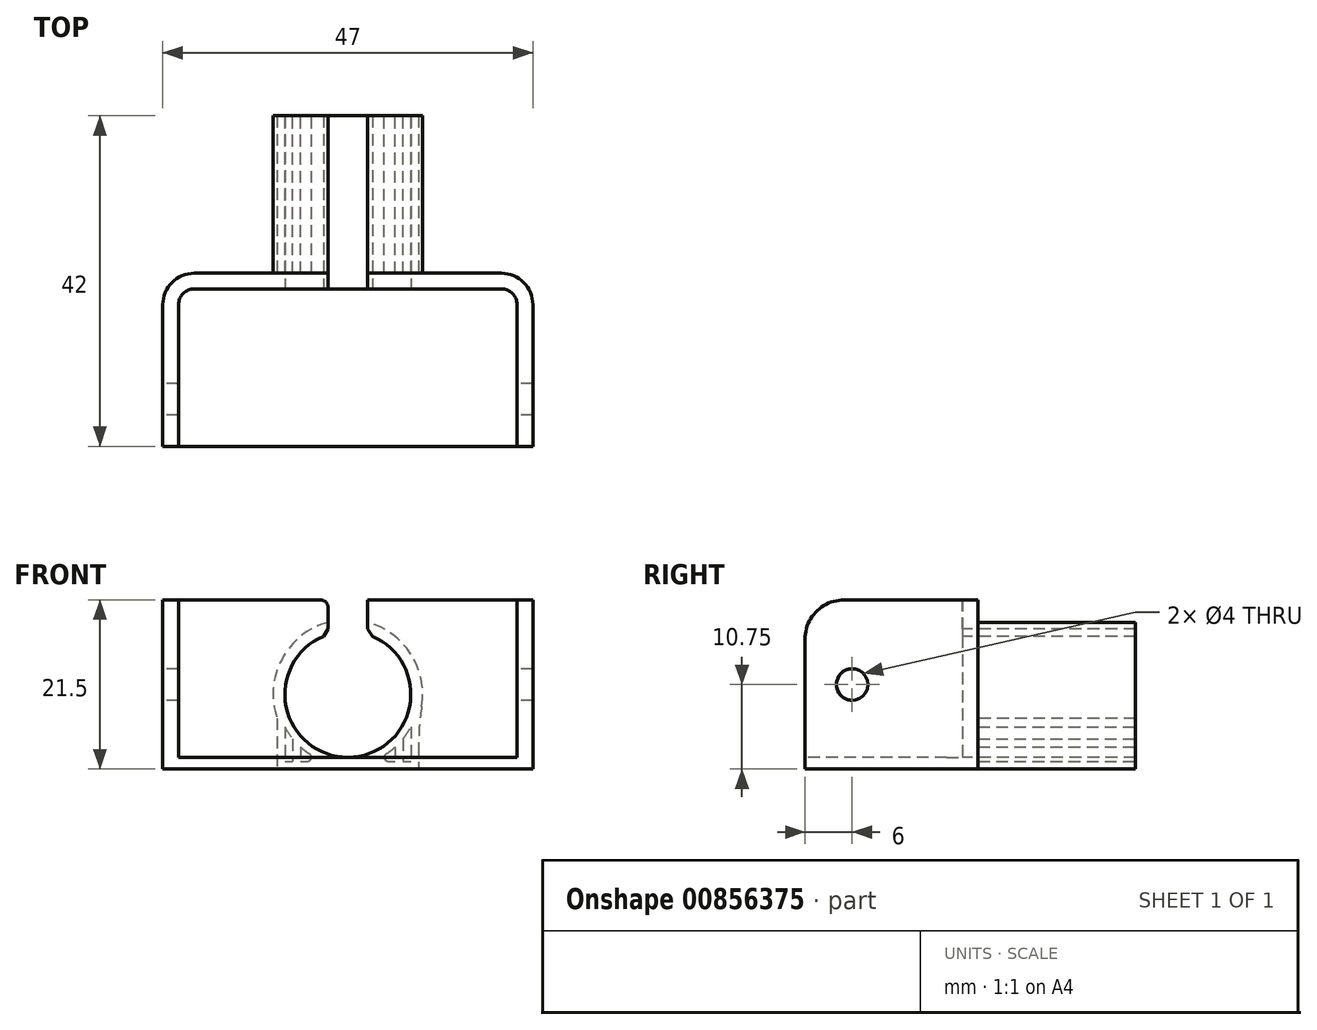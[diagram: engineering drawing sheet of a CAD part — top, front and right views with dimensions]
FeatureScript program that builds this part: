
annotation { "Feature Type Name" : "Feature", "Feature Type Description" : "" }
export const myFeature = defineFeature(function(context is Context, id is Id, definition is map)
    precondition{}
    {
        {
            var Q0;
            Q0=qCreatedBy(makeId("Top.planeOp"),FACE);
            var sketch = newSketch(context, id + "F0", { "sketchPlane" : qUnion([Q0])});
            skLineSegment(sketch, "E0.bottom", {"start": v(21.5, 20) * mm, "end": v(-21.5, 20) * mm});
            skLineSegment(sketch, "E0.left", {"start": v(21.5, 20) * mm, "end": v(21.5, 0) * mm});
            skLineSegment(sketch, "E0.right", {"start": v(-21.5, 20) * mm, "end": v(-21.5, 0) * mm});
            skPoint(sketch, "E0.middle", {"position": v(0, 0) * mm});
            skLineSegment(sketch, "E1.bottom", {"start": v(23.5, 22) * mm, "end": v(-23.5, 22) * mm});
            skLineSegment(sketch, "E1.left", {"start": v(23.5, 22) * mm, "end": v(23.5, 0) * mm});
            skLineSegment(sketch, "E1.right", {"start": v(-23.5, 22) * mm, "end": v(-23.5, 0) * mm});
            skLineSegment(sketch, "E2", {"start": v(-23.5, 0) * mm, "end": v(-21.5, 0) * mm});
            skPoint(sketch, "E0.top.end.orphan", {"position": v(-21.5, -20) * mm});
            skPoint(sketch, "E1.top.end.orphan", {"position": v(-23.5, -22) * mm});
            skPoint(sketch, "E3.orphan", {"position": v(21.5, -20) * mm});
            skPoint(sketch, "E4.orphan", {"position": v(23.5, -22) * mm});
            skLineSegment(sketch, "E5.trimOffspring", {"start": v(21.5, 0) * mm, "end": v(23.5, 0) * mm});
            skSolve(sketch);
        }
        {
            var Q0;
            Q0=makeQuery(id+"F0.imprint","IMPRINT",FACE,{"disambiguationData":[TD([[makeQuery(id+"F0.imprint","IMPRINT",EDGE,{"derivedFrom":sQuery(id+"F0.wireOp",EDGE,"E0.bottom")}),-1.0]])]});
            extrude(context, id + "F1", {"entities" : qUnion([Q0]), "depth" : 20 * mm, "offsetDistance" : 25 * mm});
        }
        {
            var Q0;
            Q0=makeQuery(id+"F1.opExtrude","SWEPT_EDGE",EDGE,{"disambiguationData":[OSD([sQuery(id+"F0.wireOp",EDGE,"E0.bottom"),sQuery(id+"F0.wireOp",EDGE,"E0.right")])]});
            var Q1;
            Q1=makeQuery(id+"F1.opExtrude","SWEPT_EDGE",EDGE,{"disambiguationData":[OSD([sQuery(id+"F0.wireOp",EDGE,"E0.bottom"),sQuery(id+"F0.wireOp",EDGE,"E0.left")])]});
            fillet(context, id + "F2", {"entities" : qUnion([Q0, Q1]), "radius" : 2 * mm, "tangentPropagation" : true, "allowEdgeOverflow" : false});
        }
        {
            var Q0;
            Q0=makeQuery(id+"F1.opExtrude","SWEPT_EDGE",EDGE,{"disambiguationData":[OSD([sQuery(id+"F0.wireOp",EDGE,"E1.bottom"),sQuery(id+"F0.wireOp",EDGE,"E1.right")])]});
            var Q1;
            Q1=makeQuery(id+"F1.opExtrude","SWEPT_EDGE",EDGE,{"disambiguationData":[OSD([sQuery(id+"F0.wireOp",EDGE,"E1.bottom"),sQuery(id+"F0.wireOp",EDGE,"E1.left")])]});
            fillet(context, id + "F3", {"entities" : qUnion([Q0, Q1]), "radius" : 4 * mm, "tangentPropagation" : true, "allowEdgeOverflow" : false});
        }
        {
            var Q0;
            Q0=makeQuery(id+"F1.opExtrude","CAP_FACE",FACE,{"disambiguationData":[OSD([sQuery(id+"F0.wireOp",EDGE,"E0.bottom"),sQuery(id+"F0.wireOp",EDGE,"E0.left"),sQuery(id+"F0.wireOp",EDGE,"E0.right"),sQuery(id+"F0.wireOp",EDGE,"E1.bottom"),sQuery(id+"F0.wireOp",EDGE,"E1.left"),sQuery(id+"F0.wireOp",EDGE,"E1.right"),sQuery(id+"F0.wireOp",EDGE,"E2"),sQuery(id+"F0.wireOp",EDGE,"E5.trimOffspring")])],"isStart":true});
            var sketch = newSketch(context, id + "F4", { "sketchPlane" : qUnion([Q0])});
            skLineSegment(sketch, "E6.0", {"start": v(23.5, -18) * mm, "end": v(23.5, 0) * mm});
            skArc(sketch, "E6.1", {"start": v(19.5, -22) * mm, "mid": v(22.33, -20.83) * mm, "end": v(23.5, -18) * mm});
            skLineSegment(sketch, "E6.2", {"start": v(19.5, -22) * mm, "end": v(-19.5, -22) * mm});
            skArc(sketch, "E6.3", {"start": v(-23.5, -18) * mm, "mid": v(-22.33, -20.83) * mm, "end": v(-19.5, -22) * mm});
            skLineSegment(sketch, "E6.4", {"start": v(-23.5, -18) * mm, "end": v(-23.5, 0) * mm});
            skLineSegment(sketch, "E7", {"start": v(23.5, 0) * mm, "end": v(-23.5, 0) * mm});
            skPoint(sketch, "E8.orphan", {"position": v(23.5, 0) * mm});
            skPoint(sketch, "E9.orphan", {"position": v(-23.5, 0) * mm});
            skSolve(sketch);
        }
        {
            var Q0;
            {var subQ0=sQuery(id+"F0.wireOp",EDGE,"E0.bottom");Q0=makeQuery(id+"F4.imprint","IMPRINT",FACE,{"disambiguationData":[TD([[makeQuery(id+"F4.imprint","IMPRINT",EDGE,{"derivedFrom":makeQuery(id+"F1.opExtrude","CAP_EDGE",EDGE,{"disambiguationData":[OSD([subQ0])],"isStart":true})}),-1.0]])]});}
            var Q1;
            {var subQ11=sQuery(id+"F4.wireOp",EDGE,"E6.0");Q1=makeQuery(id+"F4.imprint","IMPRINT",FACE,{"disambiguationData":[TD([[makeQuery(id+"F4.imprint","IMPRINT",EDGE,{"derivedFrom":subQ11}),1.0]])]});}
            extrude(context, id + "F5", {"entities" : qUnion([Q0, Q1]), "operationType" : NewBodyOperationType.ADD, "depth" : 1.5 * mm, "offsetDistance" : 25 * mm});
        }
        {
            var Q0;
            Q0=makeQuery(id+"F5.boolean.opBoolean","MERGE",FACE,{"derivedFrom":[makeQuery(id+"F1.opExtrude","SWEPT_FACE",FACE,{"disambiguationData":[OSD([sQuery(id+"F0.wireOp",EDGE,"E1.bottom")])]}),makeQuery(id+"F5.opExtrude","SWEPT_FACE",FACE,{"disambiguationData":[OSD([sQuery(id+"F4.wireOp",EDGE,"E6.2")])]})]});
            var sketch = newSketch(context, id + "F6", { "sketchPlane" : qUnion([Q0])});
            skCircle(sketch, "E10", {"center": v(0, 8) * mm, "radius": 8 * mm});
            skCircle(sketch, "E11", {"center": v(0, 8) * mm, "radius": 9.5 * mm});
            skSolve(sketch);
        }
        {
            var Q0;
            Q0=makeQuery(id+"F6.imprint","IMPRINT",FACE,{"disambiguationData":[TD([[makeQuery(id+"F6.imprint","IMPRINT",EDGE,{"derivedFrom":sQuery(id+"F6.wireOp",EDGE,"E10")}),-1.0]])]});
            extrude(context, id + "F7", {"entities" : qUnion([Q0]), "operationType" : NewBodyOperationType.ADD, "depth" : 20 * mm, "offsetDistance" : 25 * mm});
        }
        {
            var Q0;
            Q0=makeQuery(id+"F7.boolean.opBoolean","SPLIT",FACE,{"disambiguationData":[TD([makeQuery(id+"F7.opExtrude","SWEPT_FACE",FACE,{"disambiguationData":[OSD([sQuery(id+"F6.wireOp",EDGE,"E10")])]})])],"derivedFrom":makeQuery(id+"F5.boolean.opBoolean","MERGE",FACE,{"derivedFrom":[makeQuery(id+"F1.opExtrude","SWEPT_FACE",FACE,{"disambiguationData":[OSD([sQuery(id+"F0.wireOp",EDGE,"E1.bottom")])]}),makeQuery(id+"F5.opExtrude","SWEPT_FACE",FACE,{"disambiguationData":[OSD([sQuery(id+"F4.wireOp",EDGE,"E6.2")])]})]})});
            extrude(context, id + "F8", {"entities" : qUnion([Q0]), "operationType" : NewBodyOperationType.REMOVE, "oppositeDirection" : true, "depth" : 25 * mm, "offsetDistance" : 25 * mm});
        }
        {
            var Q0;
            Q0=makeQuery(id+"F1.opExtrude","CAP_FACE",FACE,{"disambiguationData":[OSD([sQuery(id+"F0.wireOp",EDGE,"E0.bottom"),sQuery(id+"F0.wireOp",EDGE,"E0.left"),sQuery(id+"F0.wireOp",EDGE,"E0.right"),sQuery(id+"F0.wireOp",EDGE,"E1.bottom"),sQuery(id+"F0.wireOp",EDGE,"E1.left"),sQuery(id+"F0.wireOp",EDGE,"E1.right"),sQuery(id+"F0.wireOp",EDGE,"E2"),sQuery(id+"F0.wireOp",EDGE,"E5.trimOffspring")])],"isStart":false});
            var sketch = newSketch(context, id + "F9", { "sketchPlane" : qUnion([Q0])});
            skLineSegment(sketch, "E12.bottom", {"start": v(-2.5, 16.96) * mm, "end": v(2.5, 16.96) * mm});
            skLineSegment(sketch, "E12.top", {"start": v(-2.5, 57.99) * mm, "end": v(2.5, 57.99) * mm});
            skLineSegment(sketch, "E12.left", {"start": v(-2.5, 16.96) * mm, "end": v(-2.5, 57.99) * mm});
            skLineSegment(sketch, "E12.right", {"start": v(2.5, 16.96) * mm, "end": v(2.5, 57.99) * mm});
            skPoint(sketch, "E12.middle", {"position": v(0, 37.47) * mm});
            skSolve(sketch);
        }
        {
            var Q0;
            {var subQ0=sQuery(id+"F9.wireOp",EDGE,"E12.top");Q0=makeQuery(id+"F9.imprint","IMPRINT",FACE,{"disambiguationData":[TD([[makeQuery(id+"F9.imprint","IMPRINT",EDGE,{"derivedFrom":subQ0}),-1.0]])]});}
            var Q1;
            {var subQ0=sQuery(id+"F9.wireOp",EDGE,"E12.bottom");Q1=makeQuery(id+"F9.imprint","IMPRINT",FACE,{"disambiguationData":[TD([[makeQuery(id+"F9.imprint","IMPRINT",EDGE,{"derivedFrom":subQ0}),1.0]])]});}
            var Q2;
            {var subQ0=sQuery(id+"F9.wireOp",EDGE,"E12.left");var subQ1=makeQuery(id+"F1.opExtrude","CAP_EDGE",EDGE,{"disambiguationData":[OSD([sQuery(id+"F0.wireOp",EDGE,"E0.bottom")])],"isStart":false});var subQ2=makeQuery(id+"F9.imprint","INTERSECT",VERTEX,{"derivedFrom":[subQ1,subQ0]});Q2=makeQuery(id+"F9.imprint","IMPRINT",FACE,{"disambiguationData":[TD([[makeQuery(id+"F9.imprint","IMPRINT",EDGE,{"disambiguationData":[TD([[subQ2,-1.0]])],"derivedFrom":subQ0}),-1.0]])]});}
            extrude(context, id + "F10", {"entities" : qUnion([Q0, Q1, Q2]), "operationType" : NewBodyOperationType.REMOVE, "oppositeDirection" : true, "depth" : 12.4 * mm, "offsetDistance" : 25 * mm});
        }
        {
            var Q0;
            {var subQ0=sQuery(id+"F6.wireOp",EDGE,"E10");Q0=makeQuery(id+"F10.boolean.opBoolean","INTERSECT",EDGE,{"derivedFrom":[makeQuery(id+"F8.boolean.opBoolean","MERGE",FACE,{"derivedFrom":[makeQuery(id+"F7.opExtrude","SWEPT_FACE",FACE,{"disambiguationData":[OSD([subQ0])]}),makeQuery(id+"F8.opExtrude","SWEPT_FACE",FACE,{"disambiguationData":[OSD([subQ0])]})]}),makeQuery(id+"F10.opExtrude","SWEPT_FACE",FACE,{"disambiguationData":[OSD([sQuery(id+"F9.wireOp",EDGE,"E12.left")])]})]});}
            var Q1;
            {var subQ0=sQuery(id+"F6.wireOp",EDGE,"E10");Q1=makeQuery(id+"F10.boolean.opBoolean","INTERSECT",EDGE,{"derivedFrom":[makeQuery(id+"F8.boolean.opBoolean","MERGE",FACE,{"derivedFrom":[makeQuery(id+"F7.opExtrude","SWEPT_FACE",FACE,{"disambiguationData":[OSD([subQ0])]}),makeQuery(id+"F8.opExtrude","SWEPT_FACE",FACE,{"disambiguationData":[OSD([subQ0])]})]}),makeQuery(id+"F10.opExtrude","SWEPT_FACE",FACE,{"disambiguationData":[OSD([sQuery(id+"F9.wireOp",EDGE,"E12.right")])]})]});}
            chamfer(context, id + "F11", {"entities" : qUnion([Q0, Q1]), "width" : 1 * mm, "tangentPropagation" : true});
        }
        {
            var Q0;
            Q0=makeQuery(id+"F10.boolean.opBoolean","COPY",EDGE,{"derivedFrom":makeQuery(id+"F10.opExtrude","CAP_EDGE",EDGE,{"disambiguationData":[OSD([sQuery(id+"F9.wireOp",EDGE,"E12.right")])],"isStart":true})});
            var Q1;
            Q1=makeQuery(id+"F10.boolean.opBoolean","COPY",EDGE,{"derivedFrom":makeQuery(id+"F10.opExtrude","CAP_EDGE",EDGE,{"disambiguationData":[OSD([sQuery(id+"F9.wireOp",EDGE,"E12.left")])],"isStart":true})});
            fillet(context, id + "F12", {"entities" : qUnion([Q0, Q1]), "radius" : 1 * mm, "tangentPropagation" : true, "allowEdgeOverflow" : false});
        }
        {
            var Q0;
            Q0=makeQuery(id+"F1.opExtrude","CAP_EDGE",EDGE,{"disambiguationData":[OSD([sQuery(id+"F0.wireOp",EDGE,"E2")])],"isStart":false});
            var Q1;
            Q1=makeQuery(id+"F1.opExtrude","CAP_EDGE",EDGE,{"disambiguationData":[OSD([sQuery(id+"F0.wireOp",EDGE,"E5.trimOffspring")])],"isStart":false});
            fillet(context, id + "F13", {"entities" : qUnion([Q0, Q1]), "radius" : 5 * mm, "tangentPropagation" : true, "allowEdgeOverflow" : false});
        }
        {
            var Q0;
            {var subQ0=sQuery(id+"F0.wireOp",EDGE,"E1.bottom");var subQ1=makeQuery(id+"F1.opExtrude","SWEPT_FACE",FACE,{"disambiguationData":[OSD([subQ0])]});var subQ3=sQuery(id+"F4.wireOp",EDGE,"E6.2");var subQ4=sQuery(id+"F4.wireOp",EDGE,"E6.1");var subQ10=makeQuery(id+"F5.opExtrude","SWEPT_FACE",FACE,{"disambiguationData":[OSD([subQ3])]});var subQ11=makeQuery(id+"F5.opExtrude","SWEPT_FACE",FACE,{"disambiguationData":[OSD([subQ4])]});Q0=makeQuery(id+"F10.boolean.opBoolean","SPLIT",FACE,{"disambiguationData":[TD([subQ11])],"derivedFrom":makeQuery(id+"F7.boolean.opBoolean","SPLIT",FACE,{"disambiguationData":[TD([subQ11])],"derivedFrom":makeQuery(id+"F5.boolean.opBoolean","MERGE",FACE,{"derivedFrom":[subQ1,subQ10]})})});}
            var sketch = newSketch(context, id + "F14", { "sketchPlane" : qUnion([Q0])});
            skLineSegment(sketch, "E13", {"start": v(-9, 4.96) * mm, "end": v(-9, -1.5) * mm});
            skLineSegment(sketch, "E14", {"start": v(-9, -1.5) * mm, "end": v(0, -1.5) * mm});
            skArc(sketch, "E15.0", {"start": v(-9, 4.96) * mm, "mid": v(0, -1.5) * mm, "end": v(9, 4.96) * mm});
            skLineSegment(sketch, "E16", {"start": v(0, 8) * mm, "end": v(0, 13.43) * mm, "construction": true});
            skLineSegment(sketch, "E17.MirrorCS", {"start": v(9, 4.96) * mm, "end": v(9, -1.5) * mm});
            skLineSegment(sketch, "E18.MirrorCS", {"start": v(9, -1.5) * mm, "end": v(0, -1.5) * mm});
            skPoint(sketch, "E19.orphan", {"position": v(-2.5, 17.17) * mm});
            skPoint(sketch, "E20.orphan", {"position": v(2.5, 17.17) * mm});
            skSolve(sketch);
        }
        {
            var Q0;
            {var subQ0=sQuery(id+"F14.wireOp",EDGE,"E13");Q0=makeQuery(id+"F14.imprint","IMPRINT",FACE,{"disambiguationData":[TD([[makeQuery(id+"F14.imprint","IMPRINT",EDGE,{"derivedFrom":subQ0}),1.0]])]});}
            var Q1;
            {var subQ2=sQuery(id+"F14.wireOp",EDGE,"E17.MirrorCS");Q1=makeQuery(id+"F14.imprint","IMPRINT",FACE,{"disambiguationData":[TD([[makeQuery(id+"F14.imprint","IMPRINT",EDGE,{"derivedFrom":subQ2}),-1.0]])]});}
            extrude(context, id + "F15", {"entities" : qUnion([Q0, Q1]), "operationType" : NewBodyOperationType.ADD, "depth" : 20 * mm, "offsetDistance" : 25 * mm});
        }
        {
            var Q0;
            {var subQ0=sQuery(id+"F14.wireOp",EDGE,"E15.0");Q0=makeQuery(id+"F15.boolean.opBoolean","MERGE",FACE,{"derivedFrom":[makeQuery(id+"F7.opExtrude","CAP_FACE",FACE,{"disambiguationData":[OSD([sQuery(id+"F6.wireOp",EDGE,"E10"),sQuery(id+"F6.wireOp",EDGE,"E11")])],"isStart":false}),makeQuery(id+"F15.opExtrude","CAP_FACE",FACE,{"disambiguationData":[OSD([sQuery(id+"F14.wireOp",EDGE,"E13"),sQuery(id+"F14.wireOp",EDGE,"E14"),subQ0])],"isStart":false}),makeQuery(id+"F15.opExtrude","CAP_FACE",FACE,{"disambiguationData":[OSD([subQ0,sQuery(id+"F14.wireOp",EDGE,"E17.MirrorCS"),sQuery(id+"F14.wireOp",EDGE,"E18.MirrorCS")])],"isStart":false})]});}
            var sketch = newSketch(context, id + "F16", { "sketchPlane" : qUnion([Q0])});
            skLineSegment(sketch, "E21.0", {"start": v(8, 3.88) * mm, "end": v(8, -0.5) * mm});
            skLineSegment(sketch, "E21.1", {"start": v(8, -0.5) * mm, "end": v(5.12, -0.5) * mm});
            skLineSegment(sketch, "E21.2", {"start": v(-8, 3.88) * mm, "end": v(-8, -0.5) * mm});
            skArc(sketch, "E22.0", {"start": v(-8, 3.88) * mm, "mid": v(-6.66, 1.94) * mm, "end": v(-4.85, 0.42) * mm});
            skLineSegment(sketch, "E23.trimOffspring", {"start": v(-5.12, -0.5) * mm, "end": v(-8, -0.5) * mm});
            skArc(sketch, "E24.trimOffspring", {"start": v(4.85, 0.42) * mm, "mid": v(6.66, 1.94) * mm, "end": v(8, 3.88) * mm});
            skLineSegment(sketch, "E25", {"start": v(-7, 2.34) * mm, "end": v(-7, -0.5) * mm});
            skLineSegment(sketch, "E26", {"start": v(-6, 1.3) * mm, "end": v(-6, -0.5) * mm});
            skPoint(sketch, "E27.visualSharp", {"position": v(-2.96, -0.5) * mm});
            skArc(sketch, "E27.filletArc", {"start": v(-5.12, -0.5) * mm, "mid": v(-4.64, -0.14) * mm, "end": v(-4.85, 0.42) * mm});
            skPoint(sketch, "E28.visualSharp", {"position": v(2.96, -0.5) * mm});
            skArc(sketch, "E28.filletArc", {"start": v(4.85, 0.42) * mm, "mid": v(4.64, -0.14) * mm, "end": v(5.12, -0.5) * mm});
            skLineSegment(sketch, "E29", {"start": v(7, 2.34) * mm, "end": v(7, -0.5) * mm});
            skLineSegment(sketch, "E30", {"start": v(6, 1.3) * mm, "end": v(6, -0.5) * mm});
            skSolve(sketch);
        }
        {
            var Q0;
            Q0=makeQuery(id+"F16.imprint","IMPRINT",FACE,{"disambiguationData":[TD([[makeQuery(id+"F16.imprint","IMPRINT",EDGE,{"derivedFrom":sQuery(id+"F16.wireOp",EDGE,"E21.2")}),1.0]])]});
            var Q1;
            Q1=makeQuery(id+"F16.imprint","IMPRINT",FACE,{"disambiguationData":[TD([[makeQuery(id+"F16.imprint","IMPRINT",EDGE,{"derivedFrom":sQuery(id+"F16.wireOp",EDGE,"E21.0")}),-1.0]])]});
            var Q2;
            {var subQ2=sQuery(id+"F16.wireOp",EDGE,"E26");Q2=makeQuery(id+"F16.imprint","IMPRINT",FACE,{"disambiguationData":[TD([[makeQuery(id+"F16.imprint","IMPRINT",EDGE,{"derivedFrom":subQ2}),1.0]])]});}
            var Q3;
            {var subQ0=sQuery(id+"F16.wireOp",EDGE,"E28.filletArc");Q3=makeQuery(id+"F16.imprint","IMPRINT",FACE,{"disambiguationData":[TD([[makeQuery(id+"F16.imprint","IMPRINT",EDGE,{"derivedFrom":subQ0}),1.0]])]});}
            extrude(context, id + "F17", {"entities" : qUnion([Q0, Q1, Q2, Q3]), "operationType" : NewBodyOperationType.REMOVE, "oppositeDirection" : true, "depth" : 20 * mm, "offsetDistance" : 25 * mm});
        }
        {
            var Q0;
            Q0=makeQuery(id+"F15.opExtrude","SWEPT_EDGE",EDGE,{"disambiguationData":[OSD([sQuery(id+"F14.wireOp",EDGE,"E15.0"),sQuery(id+"F14.wireOp",EDGE,"E17.MirrorCS")])]});
            var Q1;
            Q1=makeQuery(id+"F15.opExtrude","SWEPT_EDGE",EDGE,{"disambiguationData":[OSD([sQuery(id+"F6.wireOp",EDGE,"E11"),sQuery(id+"F14.wireOp",EDGE,"E13"),sQuery(id+"F14.wireOp",EDGE,"E15.0")])]});
            fillet(context, id + "F18", {"entities" : qUnion([Q0, Q1]), "radius" : 30 * mm, "tangentPropagation" : true, "allowEdgeOverflow" : false});
        }
        {
            var Q0;
            Q0=makeQuery(id+"F5.boolean.opBoolean","MERGE",FACE,{"derivedFrom":[makeQuery(id+"F1.opExtrude","SWEPT_FACE",FACE,{"disambiguationData":[OSD([sQuery(id+"F0.wireOp",EDGE,"E1.right")])]}),makeQuery(id+"F5.opExtrude","SWEPT_FACE",FACE,{"disambiguationData":[OSD([sQuery(id+"F4.wireOp",EDGE,"E6.4")])]})]});
            var sketch = newSketch(context, id + "F19", { "sketchPlane" : qUnion([Q0])});
            skCircle(sketch, "E31", {"center": v(-6, 9.25) * mm, "radius": 2 * mm});
            skPoint(sketch, "E31.centerSnap0", {"position": v(-18, 9.25) * mm});
            skSolve(sketch);
        }
        {
            var Q0;
            Q0=makeQuery(id+"F19.imprint","IMPRINT",FACE,{"disambiguationData":[TD([[makeQuery(id+"F19.imprint","IMPRINT",EDGE,{"derivedFrom":sQuery(id+"F19.wireOp",EDGE,"E31")}),1.0]])]});
            extrude(context, id + "F20", {"entities" : qUnion([Q0]), "operationType" : NewBodyOperationType.REMOVE, "oppositeDirection" : true, "depth" : 58 * mm, "offsetDistance" : 25 * mm});
        }
    });
